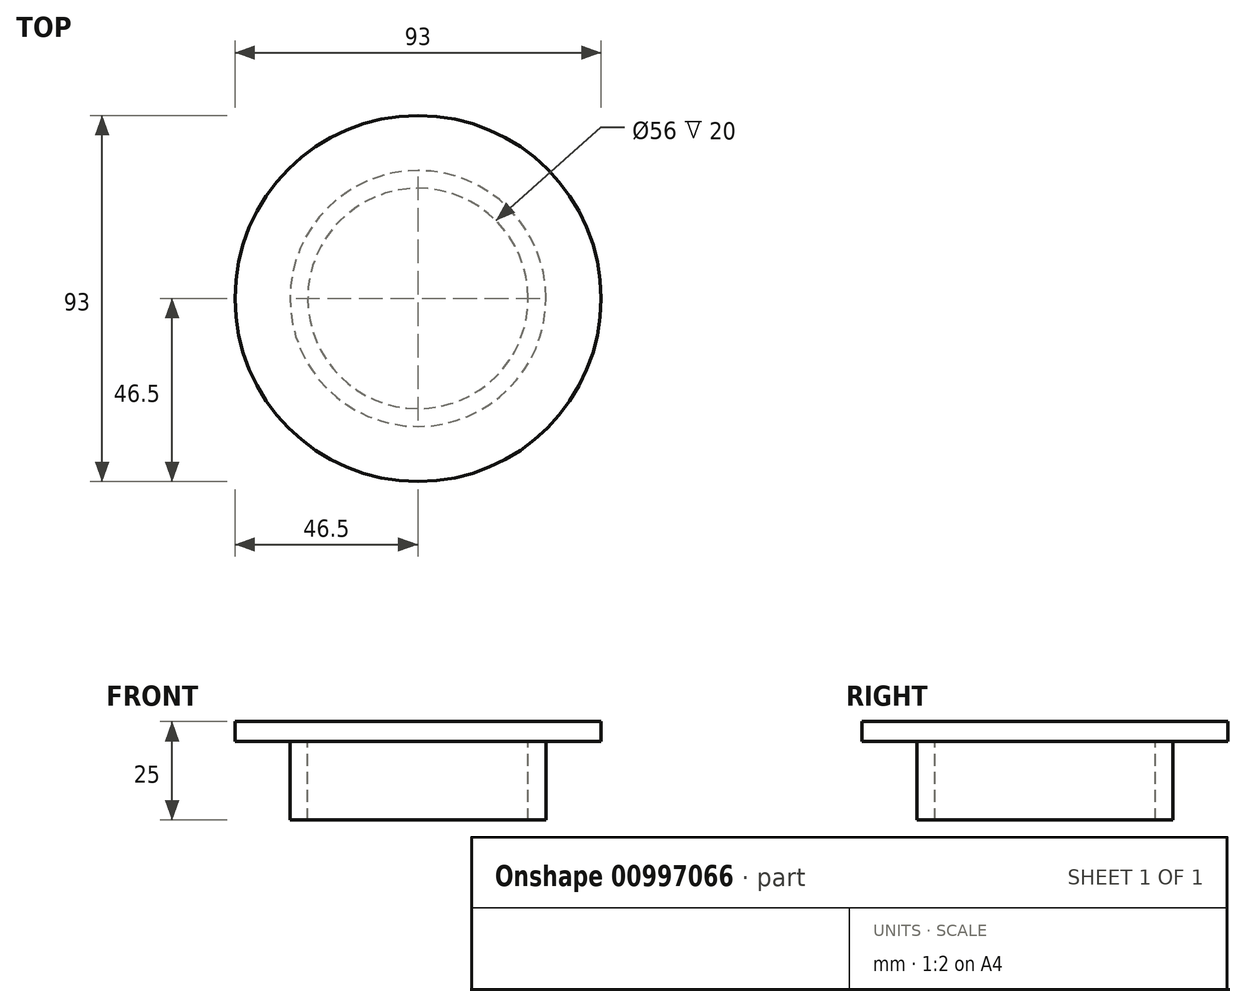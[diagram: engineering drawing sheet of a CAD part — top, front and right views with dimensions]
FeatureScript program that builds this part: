
annotation { "Feature Type Name" : "Feature", "Feature Type Description" : "" }
export const myFeature = defineFeature(function(context is Context, id is Id, definition is map)
    precondition{}
    {
        {
            var Q0;
            Q0=qCreatedBy(makeId("Front.planeOp"),FACE);
            var sketch = newSketch(context, id + "F0", { "sketchPlane" : qUnion([Q0])});
            skLineSegment(sketch, "E0", {"start": v(0, 0) * mm, "end": v(46.5, 0) * mm});
            skLineSegment(sketch, "E1", {"start": v(46.5, 0) * mm, "end": v(46.5, -5) * mm});
            skLineSegment(sketch, "E2", {"start": v(46.5, -5) * mm, "end": v(32.5, -5) * mm});
            skLineSegment(sketch, "E3", {"start": v(28, -5) * mm, "end": v(28, -25) * mm});
            skLineSegment(sketch, "E4", {"start": v(28, -25) * mm, "end": v(32.5, -25) * mm});
            skLineSegment(sketch, "E5", {"start": v(32.5, -25) * mm, "end": v(32.5, -5) * mm});
            skLineSegment(sketch, "E6.trimOffspring", {"start": v(28, -5) * mm, "end": v(0, -5) * mm});
            skLineSegment(sketch, "E7", {"start": v(0, 0) * mm, "end": v(0, -5) * mm});
            skLineSegment(sketch, "E8", {"start": v(0, 14.79) * mm, "end": v(0, -31.36) * mm, "construction": true});
            skSolve(sketch);
        }
        {
            var Q0;
            Q0=makeQuery(id+"F0.imprint","IMPRINT",FACE,{"disambiguationData":[TD([[makeQuery(id+"F0.imprint","IMPRINT",EDGE,{"derivedFrom":sQuery(id+"F0.wireOp",EDGE,"E0")}),-1.0]])]});
            var Q1;
            Q1=sQuery(id+"F0.wireOp",EDGE,"E8");
            revolve(context, id + "F1", {"surfaceOperationType" : NewSurfaceOperationType.NEW, "entities" : qUnion([Q0]), "axis" : qUnion([Q1]), "revolveType" : RevolveType.FULL});
        }
    });
